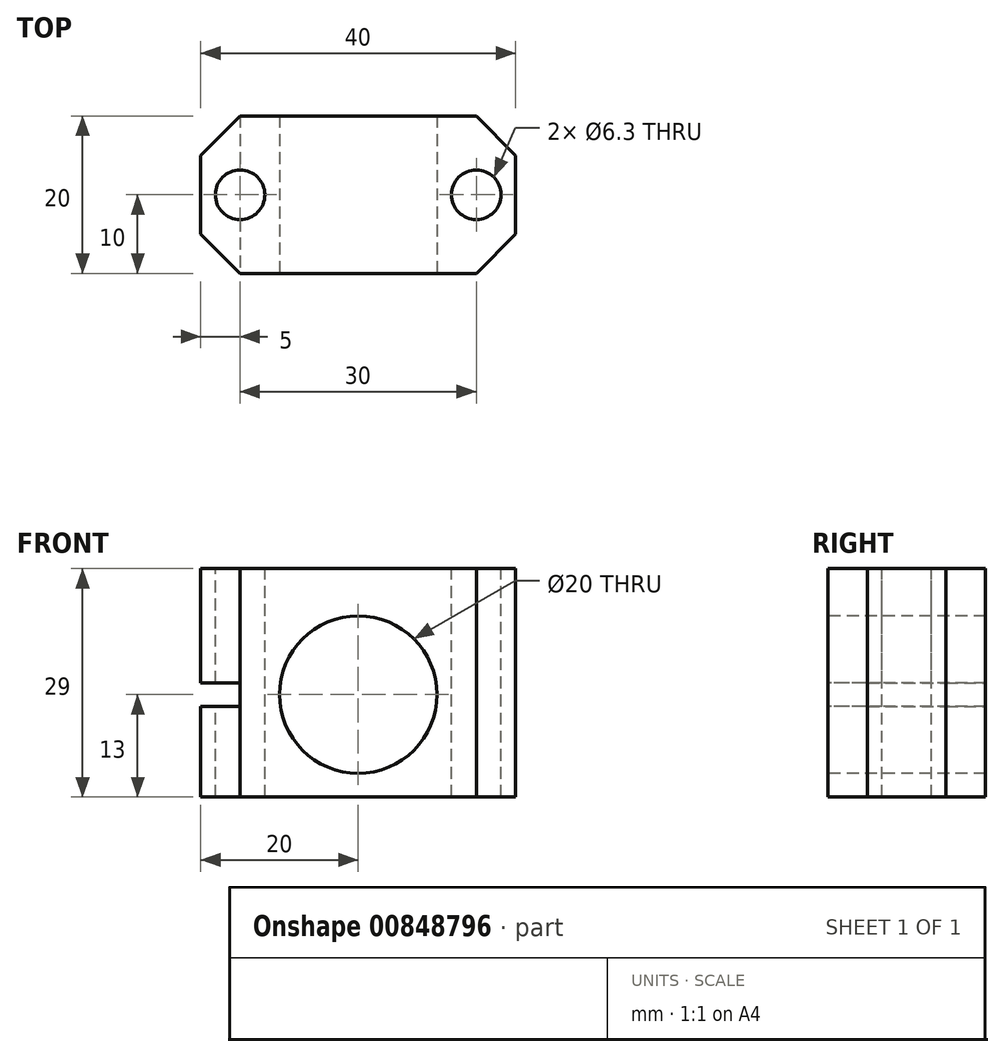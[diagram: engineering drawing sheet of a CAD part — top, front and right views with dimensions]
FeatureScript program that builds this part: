
annotation { "Feature Type Name" : "Feature", "Feature Type Description" : "" }
export const myFeature = defineFeature(function(context is Context, id is Id, definition is map)
    precondition{}
    {
        {
            var Q0;
            Q0=qCreatedBy(makeId("Top.planeOp"),FACE);
            var sketch = newSketch(context, id + "F0", { "sketchPlane" : qUnion([Q0])});
            skLineSegment(sketch, "E0.top", {"start": v(15, 10) * mm, "end": v(-15, 10) * mm});
            skLineSegment(sketch, "E0.right", {"start": v(-20, -5) * mm, "end": v(-20, 5) * mm});
            skPoint(sketch, "E0.middle", {"position": v(0, 0) * mm});
            skLineSegment(sketch, "E1", {"start": v(-20, 5) * mm, "end": v(-15, 10) * mm});
            skLineSegment(sketch, "E2.MirrorCS", {"start": v(-20, -5) * mm, "end": v(-15, -10) * mm});
            skLineSegment(sketch, "E3.MirrorCS", {"start": v(20, 5) * mm, "end": v(15, 10) * mm});
            skLineSegment(sketch, "E4.MirrorCS", {"start": v(20, -5) * mm, "end": v(15, -10) * mm});
            skLineSegment(sketch, "E5.MirrorCS", {"start": v(20, 5) * mm, "end": v(20, -5) * mm});
            skLineSegment(sketch, "E6", {"start": v(-15, -10) * mm, "end": v(15, -10) * mm});
            skSolve(sketch);
        }
        {
            var Q0;
            Q0=makeQuery(id+"F0.imprint","IMPRINT",FACE,{"disambiguationData":[TD([[makeQuery(id+"F0.imprint","IMPRINT",EDGE,{"derivedFrom":sQuery(id+"F0.wireOp",EDGE,"E0.top")}),1.0]])]});
            extrude(context, id + "F1", {"entities" : qUnion([Q0]), "depth" : 29 * mm, "offsetDistance" : 25 * mm});
        }
        {
            var Q0;
            Q0=makeQuery(id+"F1.opExtrude","SWEPT_FACE",FACE,{"disambiguationData":[OSD([sQuery(id+"F0.wireOp",EDGE,"E6")])]});
            var sketch = newSketch(context, id + "F2", { "sketchPlane" : qUnion([Q0])});
            skCircle(sketch, "E7", {"center": v(0, 13) * mm, "radius": 10 * mm});
            skSolve(sketch);
        }
        {
            var Q0;
            Q0=makeQuery(id+"F2.imprint","IMPRINT",FACE,{"disambiguationData":[TD([[makeQuery(id+"F2.imprint","IMPRINT",EDGE,{"derivedFrom":sQuery(id+"F2.wireOp",EDGE,"E7")}),1.0]])]});
            extrude(context, id + "F3", {"entities" : qUnion([Q0]), "operationType" : NewBodyOperationType.REMOVE, "endBound" : BoundingType.THROUGH_ALL, "oppositeDirection" : true, "depth" : 25 * mm, "offsetDistance" : 25 * mm});
        }
        {
            var Q0;
            Q0=makeQuery(id+"F1.opExtrude","SWEPT_FACE",FACE,{"disambiguationData":[OSD([sQuery(id+"F0.wireOp",EDGE,"E6")])]});
            var sketch = newSketch(context, id + "F4", { "sketchPlane" : qUnion([Q0])});
            skLineSegment(sketch, "E8", {"start": v(0, 13) * mm, "end": v(-29.23, 13) * mm, "construction": true});
            skLineSegment(sketch, "E9.bottom", {"start": v(-4.61, 11.5) * mm, "end": v(-24.61, 11.5) * mm});
            skLineSegment(sketch, "E9.top", {"start": v(-4.61, 14.5) * mm, "end": v(-24.61, 14.5) * mm});
            skLineSegment(sketch, "E9.left", {"start": v(-4.61, 11.5) * mm, "end": v(-4.61, 14.5) * mm});
            skLineSegment(sketch, "E9.right", {"start": v(-24.61, 11.5) * mm, "end": v(-24.61, 14.5) * mm});
            skPoint(sketch, "E9.middle", {"position": v(-14.61, 13) * mm});
            skSolve(sketch);
        }
        {
            var Q0;
            {var subQ0=sQuery(id+"F4.wireOp",EDGE,"E9.right");Q0=makeQuery(id+"F4.imprint","IMPRINT",FACE,{"disambiguationData":[TD([[makeQuery(id+"F4.imprint","IMPRINT",EDGE,{"derivedFrom":subQ0}),-1.0]])]});}
            var Q1;
            {var subQ0=sQuery(id+"F4.wireOp",EDGE,"E9.left");Q1=makeQuery(id+"F4.imprint","IMPRINT",FACE,{"disambiguationData":[TD([[makeQuery(id+"F4.imprint","IMPRINT",EDGE,{"derivedFrom":subQ0}),1.0]])]});}
            var Q2;
            {var subQ0=sQuery(id+"F4.wireOp",EDGE,"E9.bottom");var subQ3=makeQuery(id+"F3.boolean.opBoolean","COPY",EDGE,{"derivedFrom":makeQuery(id+"F3.opExtrude","CAP_EDGE",EDGE,{"disambiguationData":[OSD([sQuery(id+"F2.wireOp",EDGE,"E7")])],"isStart":true})});var subQ4=makeQuery(id+"F4.imprint","INTERSECT",VERTEX,{"derivedFrom":[subQ3,subQ0]});Q2=makeQuery(id+"F4.imprint","IMPRINT",FACE,{"disambiguationData":[TD([[makeQuery(id+"F4.imprint","IMPRINT",EDGE,{"disambiguationData":[TD([[subQ4,1.0]])],"derivedFrom":subQ3}),-1.0]])]});}
            extrude(context, id + "F5", {"entities" : qUnion([Q0, Q1, Q2]), "operationType" : NewBodyOperationType.REMOVE, "endBound" : BoundingType.THROUGH_ALL, "oppositeDirection" : true, "depth" : 25 * mm, "offsetDistance" : 25 * mm});
        }
        {
            var Q0;
            Q0=makeQuery(id+"F1.opExtrude","CAP_FACE",FACE,{"disambiguationData":[OSD([sQuery(id+"F0.wireOp",EDGE,"E0.top"),sQuery(id+"F0.wireOp",EDGE,"E0.right"),sQuery(id+"F0.wireOp",EDGE,"E1"),sQuery(id+"F0.wireOp",EDGE,"E2.MirrorCS"),sQuery(id+"F0.wireOp",EDGE,"E3.MirrorCS"),sQuery(id+"F0.wireOp",EDGE,"E4.MirrorCS"),sQuery(id+"F0.wireOp",EDGE,"E5.MirrorCS"),sQuery(id+"F0.wireOp",EDGE,"E6")])],"isStart":false});
            var sketch = newSketch(context, id + "F6", { "sketchPlane" : qUnion([Q0])});
            skPoint(sketch, "E10", {"position": v(-15, 0) * mm});
            skPoint(sketch, "E11.MirrorP", {"position": v(15, 0) * mm});
            skSolve(sketch);
        }
        {
            var Q0;
            Q0=sQuery(id+"F6.wireOp",VERTEX,"E10");
            var Q1;
            Q1=sQuery(id+"F6.wireOp",VERTEX,"E11.MirrorP");
            var Q2;
            Q2=makeQuery(id+"F1.opExtrude","SWEPT_BODY",BODY,{"disambiguationData":[OSD([sQuery(id+"F0.wireOp",EDGE,"E0.top"),sQuery(id+"F0.wireOp",EDGE,"E0.right"),sQuery(id+"F0.wireOp",EDGE,"E1"),sQuery(id+"F0.wireOp",EDGE,"E2.MirrorCS"),sQuery(id+"F0.wireOp",EDGE,"E3.MirrorCS"),sQuery(id+"F0.wireOp",EDGE,"E4.MirrorCS"),sQuery(id+"F0.wireOp",EDGE,"E5.MirrorCS"),sQuery(id+"F0.wireOp",EDGE,"E6")])]});
            hole(context, id + "F7", {"style" : HoleStyle.SIMPLE, "endStyle" : HoleEndStyle.THROUGH, "standardTappedOrClearance" : lookupTablePath({ "fit" : "Close", "standard" : "ISO", "size" : "M6", "type" : "Clearance" }), "standardBlindInLast" : lookupTablePath({ "fit" : "Close", "standard" : "ISO", "size" : "M6", "type" : "Clearance" }), "holeDiameter" : 6.3 * mm, "majorDiameter" : 6 * mm, "isTappedThrough" : true, "tappedDepth" : 2 * mm, "tapClearance" : 3, "startFromSketch" : true, "locations" : qUnion([Q0, Q1]), "scope" : qUnion([Q2])});
        }
    });
